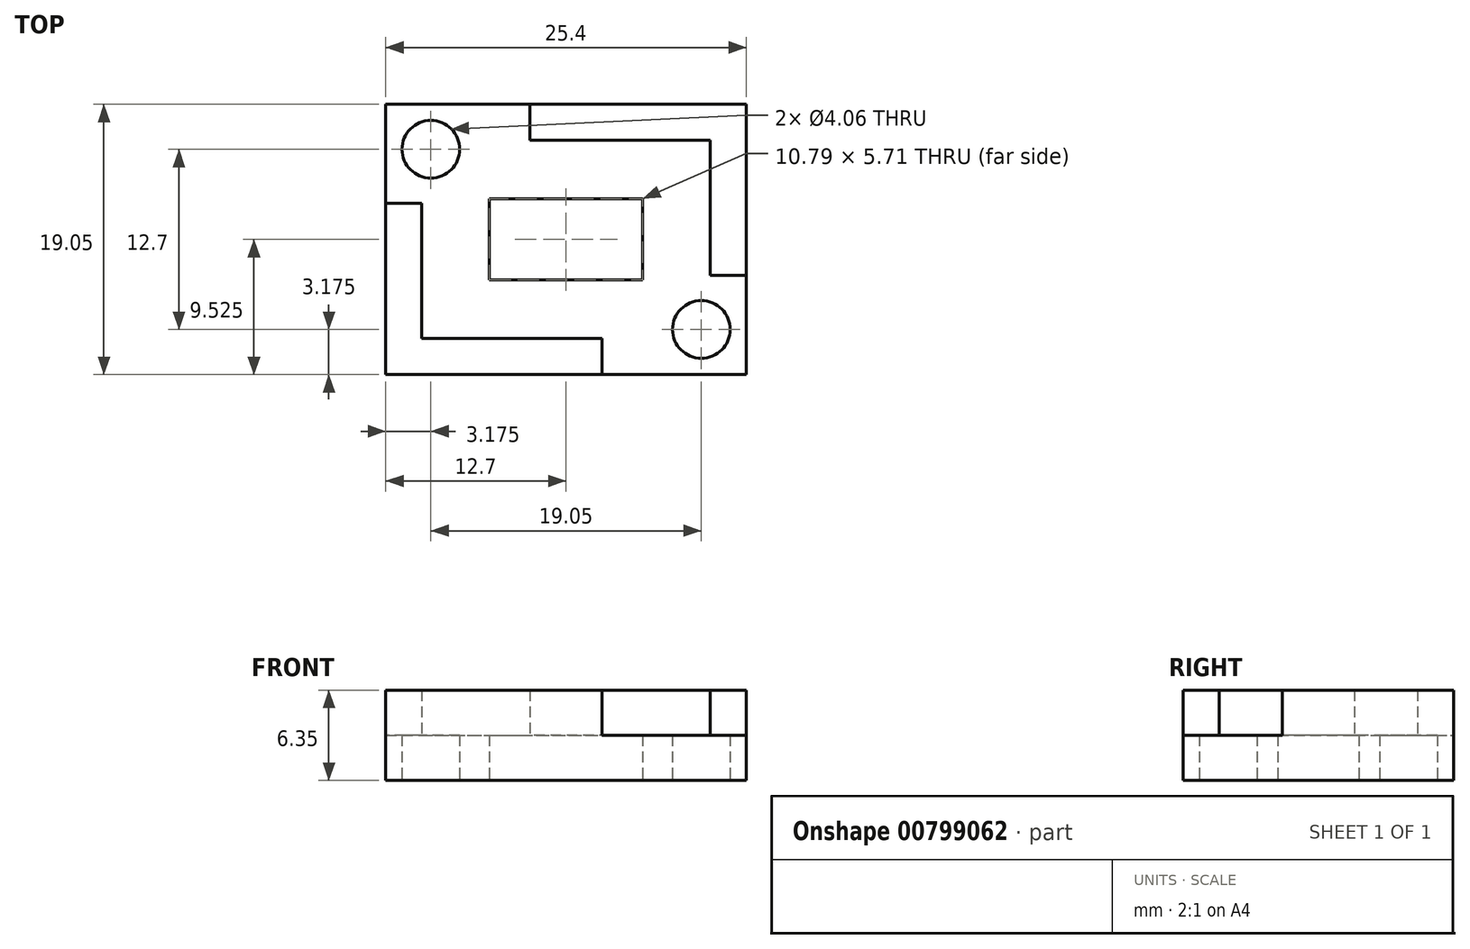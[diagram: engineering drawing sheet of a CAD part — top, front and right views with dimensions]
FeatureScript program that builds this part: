
annotation { "Feature Type Name" : "Feature", "Feature Type Description" : "" }
export const myFeature = defineFeature(function(context is Context, id is Id, definition is map)
    precondition{}
    {
        {
            var Q0;
            Q0=qCreatedBy(makeId("Top.planeOp"),FACE);
            var sketch = newSketch(context, id + "F0", { "sketchPlane" : qUnion([Q0])});
            skLineSegment(sketch, "E0.bottom", {"start": v(0, 0) * mm, "end": v(25.4, 0) * mm});
            skLineSegment(sketch, "E0.top", {"start": v(0, 19.05) * mm, "end": v(25.4, 19.05) * mm});
            skLineSegment(sketch, "E0.left", {"start": v(0, 0) * mm, "end": v(0, 19.05) * mm});
            skLineSegment(sketch, "E0.right", {"start": v(25.4, 0) * mm, "end": v(25.4, 19.05) * mm});
            skLineSegment(sketch, "E1", {"start": v(0, 9.53) * mm, "end": v(25.4, 9.53) * mm, "construction": true});
            skLineSegment(sketch, "E2", {"start": v(12.7, 19.05) * mm, "end": v(12.7, 0) * mm, "construction": true});
            skLineSegment(sketch, "E3.bottom", {"start": v(7.3, 12.38) * mm, "end": v(18.1, 12.38) * mm});
            skLineSegment(sketch, "E3.top", {"start": v(7.3, 6.67) * mm, "end": v(18.1, 6.67) * mm});
            skLineSegment(sketch, "E3.left", {"start": v(7.3, 12.38) * mm, "end": v(7.3, 6.67) * mm});
            skLineSegment(sketch, "E3.right", {"start": v(18.1, 12.38) * mm, "end": v(18.1, 6.67) * mm});
            skLineSegment(sketch, "E4", {"start": v(12.7, 12.38) * mm, "end": v(12.7, 6.67) * mm, "construction": true});
            skLineSegment(sketch, "E5", {"start": v(7.3, 9.53) * mm, "end": v(18.1, 9.53) * mm, "construction": true});
            skCircle(sketch, "E6", {"center": v(3.17, 15.88) * mm, "radius": 2.03 * mm});
            skCircle(sketch, "E7", {"center": v(22.22, 3.18) * mm, "radius": 2.03 * mm});
            skLineSegment(sketch, "E8.0", {"start": v(2.54, 2.54) * mm, "end": v(2.54, 12.06) * mm});
            skLineSegment(sketch, "E9", {"start": v(2.54, 12.06) * mm, "end": v(0, 12.06) * mm});
            skLineSegment(sketch, "E10.0", {"start": v(2.54, 2.54) * mm, "end": v(15.24, 2.54) * mm});
            skLineSegment(sketch, "E11", {"start": v(15.24, 2.54) * mm, "end": v(15.24, 0) * mm});
            skLineSegment(sketch, "E12.0", {"start": v(22.86, 16.51) * mm, "end": v(22.86, 6.99) * mm});
            skLineSegment(sketch, "E13", {"start": v(22.86, 6.99) * mm, "end": v(25.4, 6.99) * mm});
            skLineSegment(sketch, "E14.0", {"start": v(22.86, 16.51) * mm, "end": v(10.16, 16.51) * mm});
            skLineSegment(sketch, "E15", {"start": v(10.16, 16.51) * mm, "end": v(10.16, 19.05) * mm});
            skLineSegment(sketch, "E16", {"start": v(0, 12.06) * mm, "end": v(0, 0) * mm});
            skLineSegment(sketch, "E17", {"start": v(15.24, 0) * mm, "end": v(0, 0) * mm});
            skLineSegment(sketch, "E18", {"start": v(10.16, 19.05) * mm, "end": v(25.4, 19.05) * mm});
            skLineSegment(sketch, "E19", {"start": v(25.4, 6.99) * mm, "end": v(25.4, 19.05) * mm});
            skSolve(sketch);
        }
        {
            var Q0;
            Q0=makeQuery(id+"F0.imprint","IMPRINT",FACE,{"disambiguationData":[TD([[makeQuery(id+"F0.imprint","IMPRINT",EDGE,{"derivedFrom":sQuery(id+"F0.wireOp",EDGE,"E3.bottom")}),1.0]])]});
            extrude(context, id + "F1", {"entities" : qUnion([Q0]), "depth" : 3.17 * mm, "offsetDistance" : 25.4 * mm});
        }
        {
            var Q0;
            Q0=makeQuery(id+"F0.imprint","IMPRINT",FACE,{"disambiguationData":[TD([[makeQuery(id+"F0.imprint","IMPRINT",EDGE,{"derivedFrom":sQuery(id+"F0.wireOp",EDGE,"E8.0")}),1.0]])]});
            var Q1;
            Q1=makeQuery(id+"F0.imprint","IMPRINT",FACE,{"disambiguationData":[TD([[makeQuery(id+"F0.imprint","IMPRINT",EDGE,{"derivedFrom":sQuery(id+"F0.wireOp",EDGE,"E12.0")}),1.0]])]});
            extrude(context, id + "F2", {"entities" : qUnion([Q0, Q1]), "operationType" : NewBodyOperationType.ADD, "depth" : 6.35 * mm, "offsetDistance" : 25.4 * mm});
        }
    });
